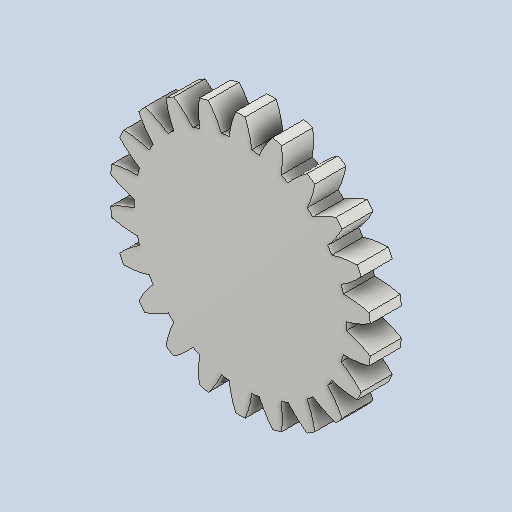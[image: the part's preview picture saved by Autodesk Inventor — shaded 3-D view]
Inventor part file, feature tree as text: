
AUTODESK INVENTOR PART (.ipt)
format: ipt  version: 2024 (Build 280153000, 153)  size: 235,520 bytes
history: native  units: mm (DEFAULTED — no unit token found)
features: plane x3, other x3, extrude x1, sketch x1
ambient origin geometry x8: Origin, YZ Plane, XZ Plane, XY Plane, X Axis, Y Axis, Z Axis, Center Point
bodies: Solid1 (feature_tree)
feature tree (8):
  extrude  "Extrusion1"  Depth=20.0mm TaperAngle=0.0deg
  plane  "Work Plane2"
  plane  "Work Plane8"
  plane  "Work Plane9"
  other  "Spur Gear"
  sketch  "Sketch1"  dims[d0=167.800152mm d1=20.0mm d2=0.0mm d3=154.0mm d4=10.0mm d5=0.0mm d16=230.0mm d17=0.0mm d34=1.427997mm d39=0.0mm d41=0.0mm d43=230.0mm d46=230.0mm d47=0.0mm d48=0.0mm]
  other  "Srf1"
  other  "Pitch Diameter"
